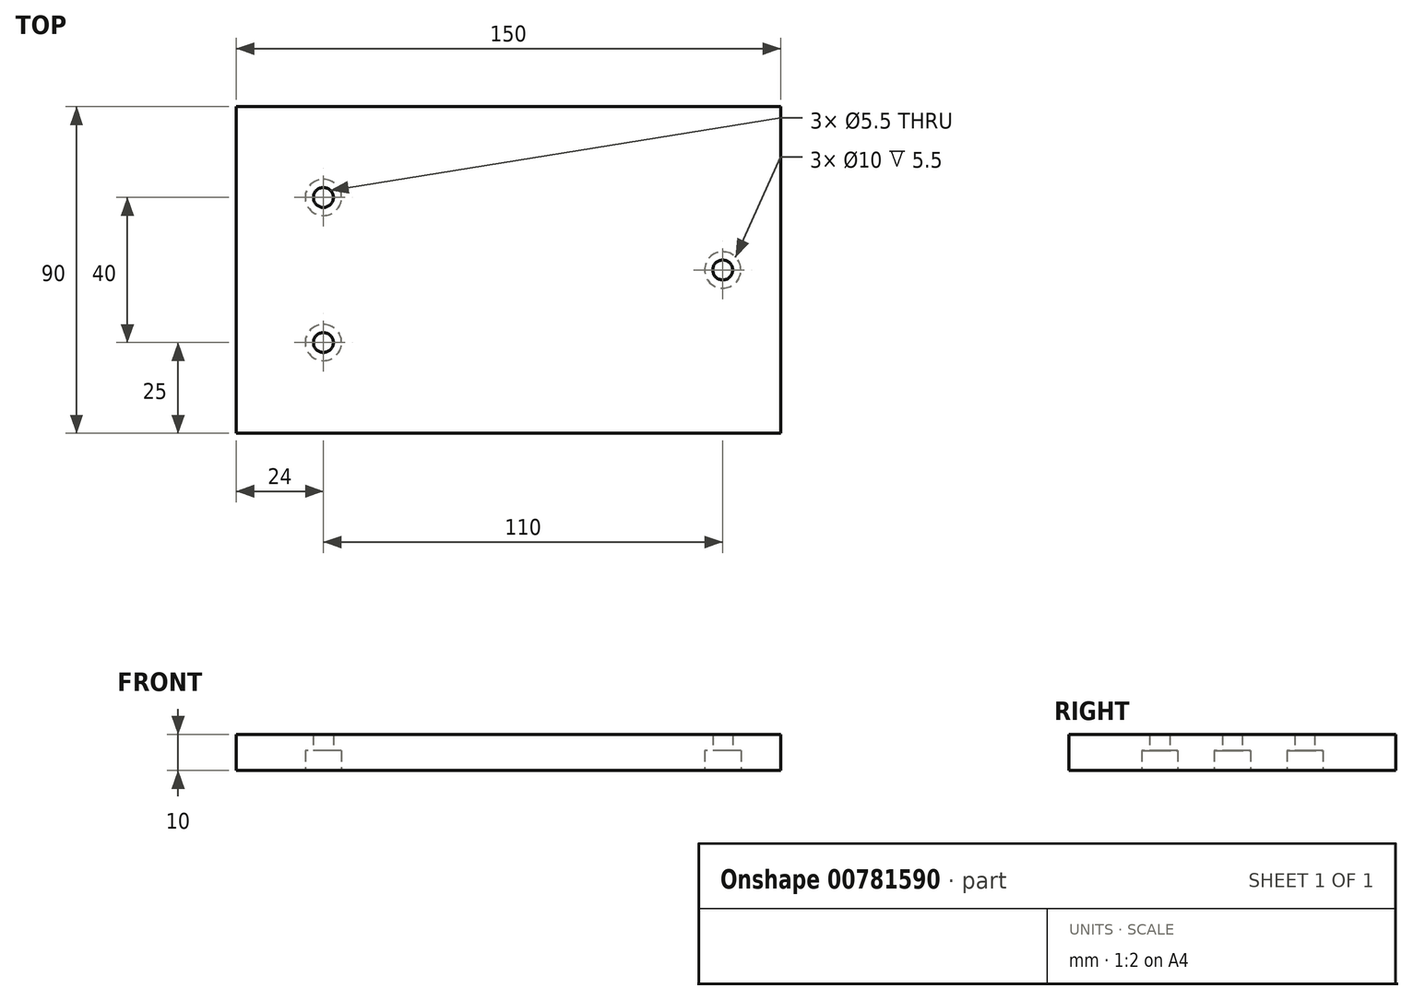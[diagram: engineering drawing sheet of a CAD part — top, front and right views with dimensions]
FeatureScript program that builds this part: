
annotation { "Feature Type Name" : "Feature", "Feature Type Description" : "" }
export const myFeature = defineFeature(function(context is Context, id is Id, definition is map)
    precondition{}
    {
        {
            var Q0;
            Q0=qCreatedBy(makeId("Top.planeOp"),FACE);
            var sketch = newSketch(context, id + "F0", { "sketchPlane" : qUnion([Q0])});
            skLineSegment(sketch, "E0.bottom", {"start": v(75, 45) * mm, "end": v(-75, 45) * mm});
            skLineSegment(sketch, "E0.top", {"start": v(75, -45) * mm, "end": v(-75, -45) * mm});
            skLineSegment(sketch, "E0.left", {"start": v(75, 45) * mm, "end": v(75, -45) * mm});
            skLineSegment(sketch, "E0.right", {"start": v(-75, 45) * mm, "end": v(-75, -45) * mm});
            skPoint(sketch, "E0.middle", {"position": v(0, 0) * mm});
            skCircle(sketch, "E1", {"center": v(-51, -20) * mm, "radius": 2.75 * mm});
            skCircle(sketch, "E2", {"center": v(59, 0) * mm, "radius": 2.75 * mm});
            skCircle(sketch, "E3", {"center": v(-51, 20) * mm, "radius": 2.75 * mm});
            skLineSegment(sketch, "E4", {"start": v(-51, -20) * mm, "end": v(-51, 20) * mm, "construction": true});
            skLineSegment(sketch, "E5", {"start": v(59, 0) * mm, "end": v(-51, 0) * mm, "construction": true});
            skLineSegment(sketch, "E6", {"start": v(59, 0) * mm, "end": v(59, -45) * mm, "construction": true});
            skLineSegment(sketch, "E7", {"start": v(59, 0) * mm, "end": v(59, 45) * mm, "construction": true});
            skCircle(sketch, "E8", {"center": v(-51, 20) * mm, "radius": 5 * mm});
            skCircle(sketch, "E9", {"center": v(-51, -20) * mm, "radius": 5 * mm});
            skCircle(sketch, "E10", {"center": v(59, 0) * mm, "radius": 5 * mm});
            skSolve(sketch);
        }
        {
            var Q0;
            Q0 = qSketchRegion(id + "F0", true);
            var Q1;
            Q1=makeQuery(id+"F0.imprint","IMPRINT",FACE,{"disambiguationData":[TD([[makeQuery(id+"F0.imprint","IMPRINT",EDGE,{"derivedFrom":sQuery(id+"F0.wireOp",EDGE,"E3")}),-1.0]])]});
            var Q2;
            Q2=makeQuery(id+"F0.imprint","IMPRINT",FACE,{"disambiguationData":[TD([[makeQuery(id+"F0.imprint","IMPRINT",EDGE,{"derivedFrom":sQuery(id+"F0.wireOp",EDGE,"E1")}),-1.0]])]});
            var Q3;
            Q3=makeQuery(id+"F0.imprint","IMPRINT",FACE,{"disambiguationData":[TD([[makeQuery(id+"F0.imprint","IMPRINT",EDGE,{"derivedFrom":sQuery(id+"F0.wireOp",EDGE,"E2")}),-1.0]])]});
            extrude(context, id + "F1", {"entities" : qUnion([Q0, Q1, Q2, Q3]), "depth" : 10 * mm, "offsetDistance" : 25 * mm});
        }
        {
            var Q0;
            Q0=makeQuery(id+"F0.imprint","IMPRINT",FACE,{"disambiguationData":[TD([[makeQuery(id+"F0.imprint","IMPRINT",EDGE,{"derivedFrom":sQuery(id+"F0.wireOp",EDGE,"E1")}),-1.0]])]});
            var Q1;
            Q1=makeQuery(id+"F0.imprint","IMPRINT",FACE,{"disambiguationData":[TD([[makeQuery(id+"F0.imprint","IMPRINT",EDGE,{"derivedFrom":sQuery(id+"F0.wireOp",EDGE,"E3")}),-1.0]])]});
            var Q2;
            Q2=makeQuery(id+"F0.imprint","IMPRINT",FACE,{"disambiguationData":[TD([[makeQuery(id+"F0.imprint","IMPRINT",EDGE,{"derivedFrom":sQuery(id+"F0.wireOp",EDGE,"E2")}),-1.0]])]});
            extrude(context, id + "F2", {"entities" : qUnion([Q0, Q1, Q2]), "operationType" : NewBodyOperationType.REMOVE, "depth" : 5.5 * mm, "offsetDistance" : 25 * mm});
        }
    });
